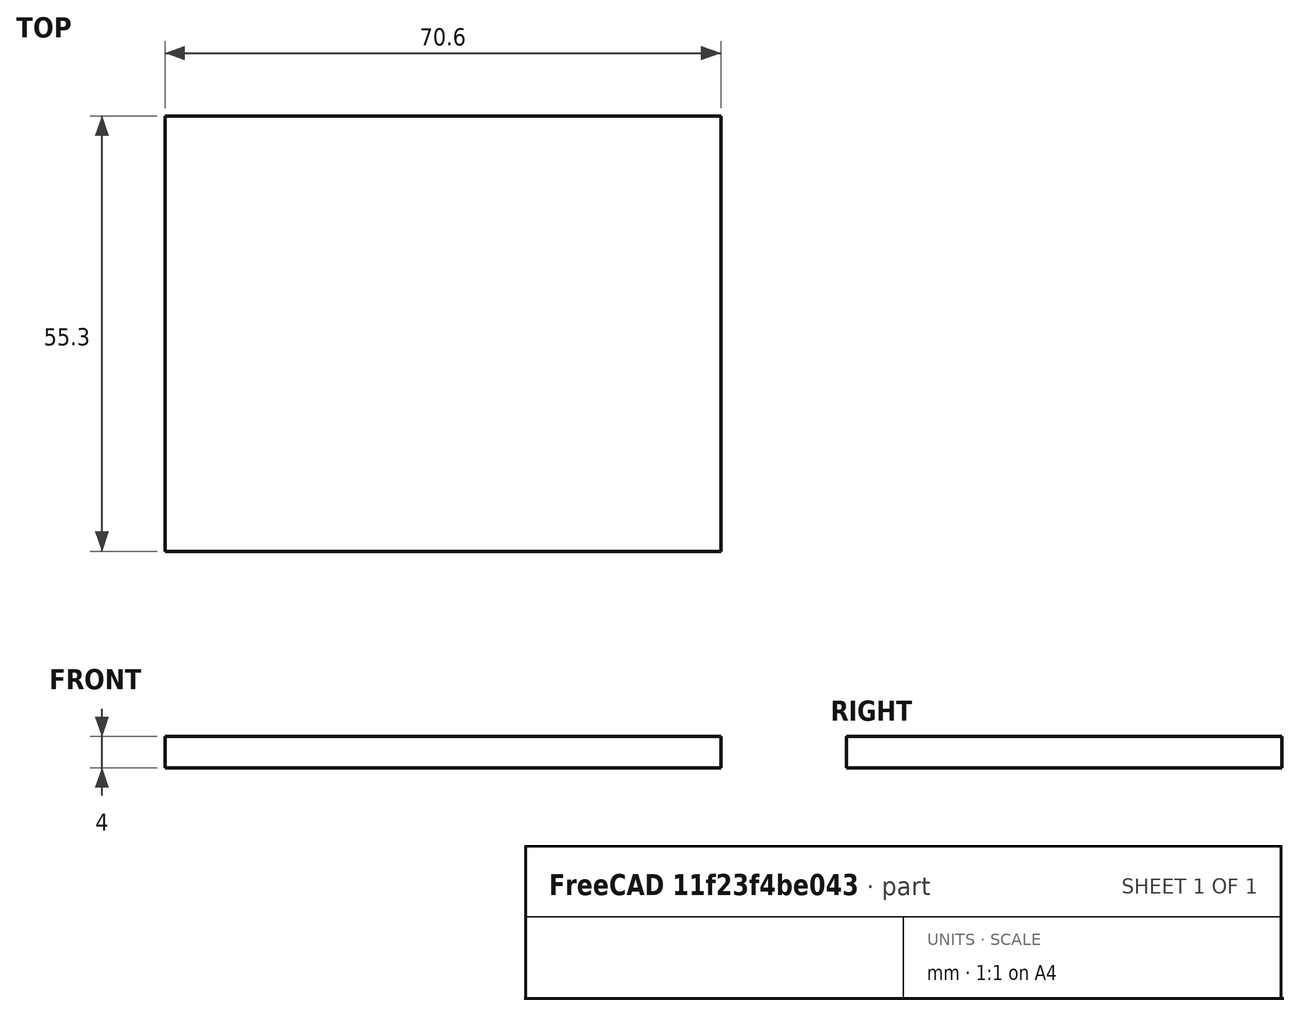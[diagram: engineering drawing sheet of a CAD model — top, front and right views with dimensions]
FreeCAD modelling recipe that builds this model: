
FCSTD DOCUMENT
Label: ArduinoUnoHoles
objects: Sketcher::SketchObject×4, PartDesign::Pad×1
note: 6 computed .brp shape members not serialized (recipe doc carries the construction recipe); baked Part::Feature solids carry a one-line shape summary decoded from their .brp

FEATURE [Sketcher::SketchObject] Sketch  label="PostHoles"
  Placement = pos=(0,0,4) rot=(0,0,1;0rad)
  sketch-geometry (5):
    g0: Circle CenterX=15 CenterY=3.5 CenterZ=0 NormalX=0 NormalY=0 NormalZ=1 Radius=1.6
    g1: Circle CenterX=16.3 CenterY=51.7 CenterZ=0 NormalX=0 NormalY=0 NormalZ=1 Radius=1.6
    g2: Circle CenterX=67.1 CenterY=36.5 CenterZ=0 NormalX=0 NormalY=0 NormalZ=1 Radius=1.6
    g3: Circle CenterX=67.1 CenterY=8.6 CenterZ=0 NormalX=0 NormalY=0 NormalZ=1 Radius=1.6
    g4: LineSegment [constr] StartX=67.1 StartY=36.5 StartZ=0 EndX=67.1 EndY=8.6 EndZ=0
  constraints (14):
    c: Radius(g0) = 1.6
    c: DistanceX(g0) = 15
    c: DistanceY(g0) = 3.5
    c: Equal(g0,g1)
    c: Equal(g1,g2)
    c: Equal(g2,g3)
    c: DistanceX(g1,g0) = -1.3
    c: DistanceX(g1,g2) = 50.8
    c: Vertical(g4)
    c: Coincident(g3,g4)
    c: Coincident(g2,g4)
    c: DistanceY(g3,g0) = -5.1
    c: DistanceY(g3,g2) = 27.9
    c: DistanceY(g1,g2) = -15.2
FEATURE [Sketcher::SketchObject] Sketch001
  sketch-geometry (4):
    g0: LineSegment StartX=0 StartY=0 StartZ=0 EndX=70.6 EndY=0 EndZ=0
    g1: LineSegment StartX=70.6 StartY=0 StartZ=0 EndX=70.6 EndY=55.3 EndZ=0
    g2: LineSegment StartX=70.6 StartY=55.3 StartZ=0 EndX=0 EndY=55.3 EndZ=0
    g3: LineSegment StartX=0 StartY=55.3 StartZ=0 EndX=0 EndY=0 EndZ=0
  constraints (12):
    c: Coincident(g0,g1)
    c: Coincident(g1,g2)
    c: Coincident(g2,g3)
    c: Coincident(g3,g0)
    c: Horizontal(g0)
    c: Horizontal(g2)
    c: Vertical(g1)
    c: Vertical(g3)
    c: DistanceY(g3) = -55.3
    c: DistanceX(g0) = 70.6
    c: DistanceX(g0) = 0
    c: DistanceY(g0) = 0
FEATURE [PartDesign::Pad] Pad
  Length = 4
  MirroredExtent = false
  Sketch = -> Sketch001
FEATURE [Sketcher::SketchObject] Sketch002  label="Posts"
  Placement = pos=(0,0,4) rot=(0,0,1;0rad)
  Support = -> Pad [Face6]
  sketch-geometry (9):
    g0: Circle CenterX=15 CenterY=3.5 CenterZ=0 NormalX=0 NormalY=0 NormalZ=1 Radius=2.5
    g1: Circle CenterX=16.3 CenterY=51.7 CenterZ=0 NormalX=0 NormalY=0 NormalZ=1 Radius=2.5
    g2: Circle CenterX=67.1 CenterY=36.5 CenterZ=0 NormalX=0 NormalY=0 NormalZ=1 Radius=2.5
    g3: Circle CenterX=67.1 CenterY=8.6 CenterZ=0 NormalX=0 NormalY=0 NormalZ=1 Radius=2.5
    g4: LineSegment [constr] StartX=67.1 StartY=36.5 StartZ=0 EndX=67.1 EndY=8.6 EndZ=0
    g5: Circle CenterX=16.3 CenterY=51.7 CenterZ=0 NormalX=0 NormalY=0 NormalZ=1 Radius=1.6
    g6: Circle CenterX=67.1 CenterY=36.5 CenterZ=0 NormalX=0 NormalY=0 NormalZ=1 Radius=1.6
    g7: Circle CenterX=67.1 CenterY=8.6 CenterZ=0 NormalX=0 NormalY=0 NormalZ=1 Radius=1.6
    g8: Circle CenterX=15 CenterY=3.5 CenterZ=0 NormalX=0 NormalY=0 NormalZ=1 Radius=1.6
  constraints (22):
    c: Radius(g0) = 2.5
    c: DistanceX(g0) = 15
    c: DistanceY(g0) = 3.5
    c: Equal(g0,g1)
    c: Equal(g1,g2)
    c: Equal(g2,g3)
    c: DistanceX(g1,g0) = -1.3
    c: DistanceX(g1,g2) = 50.8
    c: Vertical(g4)
    c: Coincident(g3,g4)
    c: Coincident(g2,g4)
    c: DistanceY(g3,g0) = -5.1
    c: DistanceY(g3,g2) = 27.9
    c: DistanceY(g1,g2) = -15.2
    c: Radius(g8) = 1.6
    c: Equal(g8,g7)
    c: Equal(g7,g6)
    c: Equal(g6,g5)
    c: Coincident(g5,g1)
    c: Coincident(g6,g2)
    c: Coincident(g7,g3)
    c: Coincident(g8,g0)
FEATURE [Sketcher::SketchObject] Sketch003  label="PostHoles001"
  Placement = pos=(0,0,4) rot=(0,0,1;0rad)
  sketch-geometry (5):
    g0: Circle CenterX=15 CenterY=3.5 CenterZ=0 NormalX=0 NormalY=0 NormalZ=1 Radius=1.6
    g1: Circle CenterX=16.3 CenterY=51.7 CenterZ=0 NormalX=0 NormalY=0 NormalZ=1 Radius=1.6
    g2: Circle CenterX=67.1 CenterY=36.5 CenterZ=0 NormalX=0 NormalY=0 NormalZ=1 Radius=1.6
    g3: Circle CenterX=67.1 CenterY=8.6 CenterZ=0 NormalX=0 NormalY=0 NormalZ=1 Radius=1.6
    g4: LineSegment [constr] StartX=67.1 StartY=36.5 StartZ=0 EndX=67.1 EndY=8.6 EndZ=0
  constraints (14):
    c: Radius(g0) = 1.6
    c: DistanceX(g0) = 15
    c: DistanceY(g0) = 3.5
    c: Equal(g0,g1)
    c: Equal(g1,g2)
    c: Equal(g2,g3)
    c: DistanceX(g1,g0) = -1.3
    c: DistanceX(g1,g2) = 50.8
    c: Vertical(g4)
    c: Coincident(g3,g4)
    c: Coincident(g2,g4)
    c: DistanceY(g3,g0) = -5.1
    c: DistanceY(g3,g2) = 27.9
    c: DistanceY(g1,g2) = -15.2
